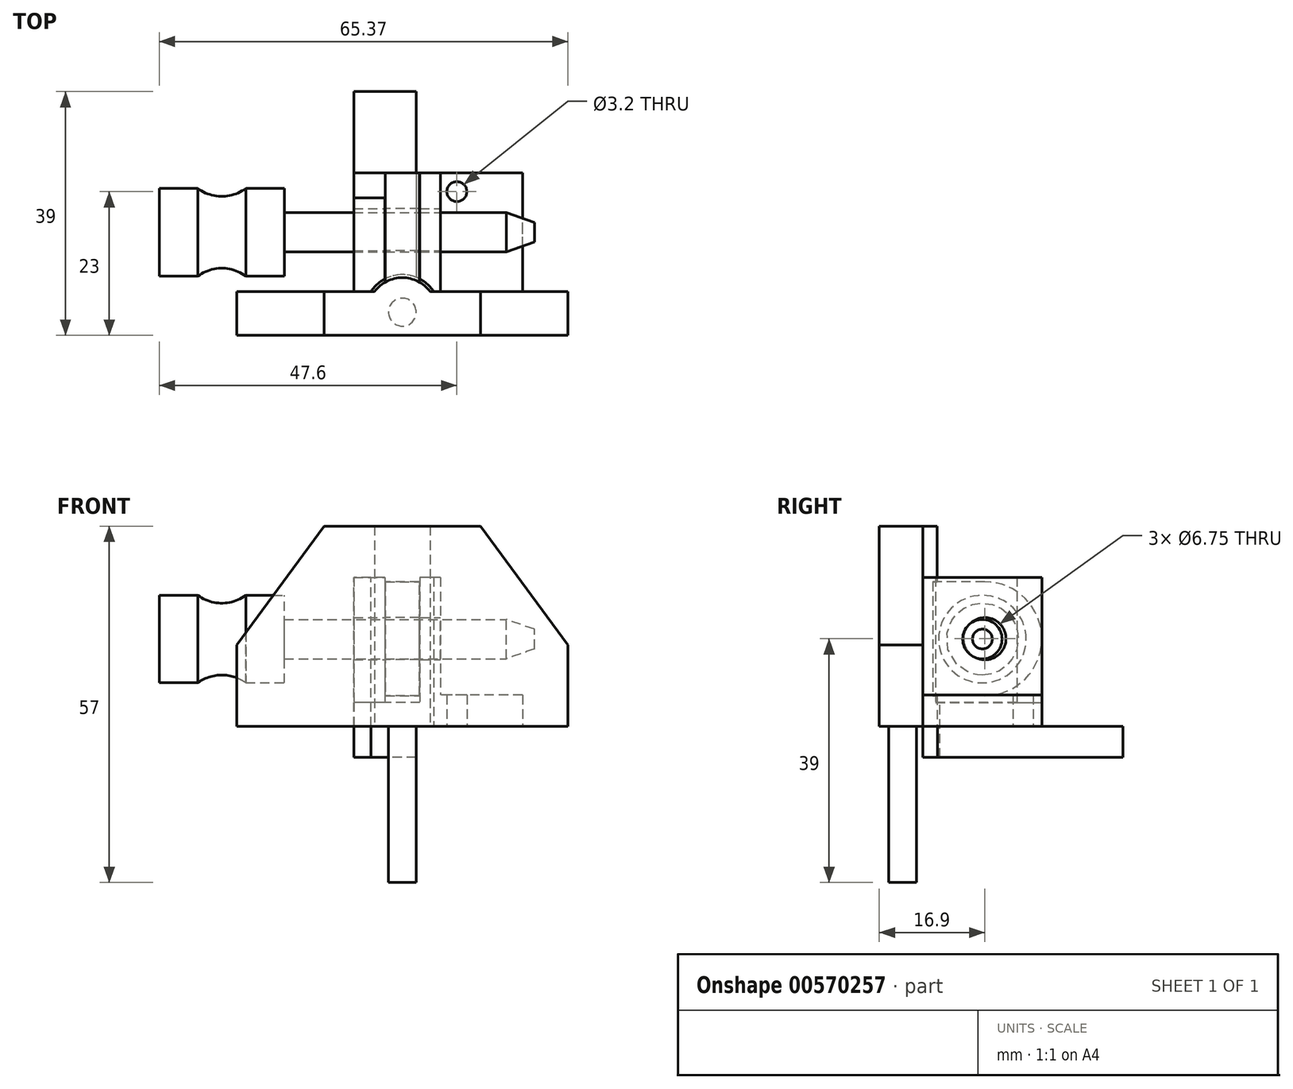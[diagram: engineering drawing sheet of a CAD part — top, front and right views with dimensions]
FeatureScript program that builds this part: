
annotation { "Feature Type Name" : "Feature", "Feature Type Description" : "" }
export const myFeature = defineFeature(function(context is Context, id is Id, definition is map)
    precondition{}
    {
        {
            var Q0;
            Q0=qCreatedBy(makeId("Top.planeOp"),FACE);
            var sketch = newSketch(context, id + "F0", { "sketchPlane" : qUnion([Q0])});
            skCircle(sketch, "E0", {"center": v(-5.72, -12.78) * mm, "radius": 2.23 * mm});
            skLineSegment(sketch, "E1.top", {"start": v(20.78, -9.5) * mm, "end": v(-32.22, -9.5) * mm});
            skLineSegment(sketch, "E1.left", {"start": v(20.78, -16.5) * mm, "end": v(20.78, -9.5) * mm});
            skLineSegment(sketch, "E1.right", {"start": v(-32.22, -16.5) * mm, "end": v(-32.22, -9.5) * mm});
            skLineSegment(sketch, "E2", {"start": v(-5.72, -9.5) * mm, "end": v(-5.72, -36.34) * mm, "construction": true});
            skLineSegment(sketch, "E3", {"start": v(-32.22, -16.5) * mm, "end": v(20.78, -16.5) * mm});
            skArc(sketch, "E4", {"start": v(-1.29, -9.5) * mm, "mid": v(-5.72, -7.26) * mm, "end": v(-10.16, -9.5) * mm});
            skSolve(sketch);
        }
        {
            var Q0;
            Q0=makeQuery(id+"F0.imprint","IMPRINT",FACE,{"disambiguationData":[TD([[makeQuery(id+"F0.imprint","IMPRINT",EDGE,{"derivedFrom":sQuery(id+"F0.wireOp",EDGE,"E0")}),-1.0]])]});
            var Q1;
            Q1=makeQuery(id+"F0.imprint","IMPRINT",FACE,{"disambiguationData":[TD([[makeQuery(id+"F0.imprint","IMPRINT",EDGE,{"derivedFrom":sQuery(id+"F0.wireOp",EDGE,"E0")}),1.0]])]});
            var Q2;
            {var subQ0=sQuery(id+"F0.wireOp",EDGE,"E4");Q2=makeQuery(id+"F0.imprint","IMPRINT",FACE,{"disambiguationData":[TD([[makeQuery(id+"F0.imprint","IMPRINT",EDGE,{"derivedFrom":subQ0}),1.0]])]});}
            extrude(context, id + "F1", {"entities" : qUnion([Q0, Q1, Q2]), "depth" : (19 + 13) * mm, "offsetDistance" : 25 * mm});
        }
        {
            var Q0;
            Q0=makeQuery(id+"F1.opExtrude","CAP_EDGE",EDGE,{"disambiguationData":[OSD([sQuery(id+"F0.wireOp",EDGE,"E1.right")])],"isStart":false});
            var Q1;
            Q1=makeQuery(id+"F1.opExtrude","CAP_EDGE",EDGE,{"disambiguationData":[OSD([sQuery(id+"F0.wireOp",EDGE,"E1.left")])],"isStart":false});
            chamfer(context, id + "F2", {"entities" : qUnion([Q0, Q1]), "chamferType" : ChamferType.TWO_OFFSETS, "width1" : 19 * mm, "oppositeDirection" : false, "width2" : 14 * mm, "tangentPropagation" : true});
        }
        {
            var Q0;
            Q0=makeQuery(id+"F0.imprint","IMPRINT",FACE,{"disambiguationData":[TD([[makeQuery(id+"F0.imprint","IMPRINT",EDGE,{"derivedFrom":sQuery(id+"F0.wireOp",EDGE,"E0")}),1.0]])]});
            extrude(context, id + "F3", {"entities" : qUnion([Q0]), "operationType" : NewBodyOperationType.ADD, "oppositeDirection" : true, "depth" : 25 * mm, "offsetDistance" : 25 * mm});
        }
        {
            var Q0;
            Q0=qCreatedBy(makeId("Right.planeOp"),FACE);
            var Q1;
            Q1=sQuery(id+"F0.wireOp",VERTEX,"E0.center");
            cPlane(context, id + "F4", {"entities" : qUnion([Q0, Q1]), "cplaneType" : CPlaneType.PLANE_POINT, "offset" : 25 * mm, "oppositeDirection" : true, "width" : 150 * mm, "height" : 150 * mm});
        }
        {
            var Q0;
            Q0=qCreatedBy(id+"F4.planeOp",FACE);
            var sketch = newSketch(context, id + "F5", { "sketchPlane" : qUnion([Q0])});
            skLineSegment(sketch, "E5.1", {"start": v(-16.5, 0) * mm, "end": v(-9.5, 0) * mm});
            skLineSegment(sketch, "E6.bottom", {"start": v(0.4, 23.1) * mm, "end": v(-16.5, 23.1) * mm});
            skLineSegment(sketch, "E6.top", {"start": v(0.4, 4) * mm, "end": v(-16.5, 4) * mm});
            skArc(sketch, "E7", {"start": v(0.4, 4.9) * mm, "mid": v(9.5, 14) * mm, "end": v(0.4, 23.1) * mm});
            skCircle(sketch, "E8", {"center": v(0.4, 14) * mm, "radius": 3.38 * mm});
            skLineSegment(sketch, "E9.0", {"start": v(-16.5, 13) * mm, "end": v(-16.5, 0) * mm});
            skLineSegment(sketch, "E9.1", {"start": v(-16.5, 13) * mm, "end": v(-16.5, 32) * mm});
            skLineSegment(sketch, "E10.0", {"start": v(0.4, 4.9) * mm, "end": v(-16.5, 4.9) * mm});
            skLineSegment(sketch, "E11.0", {"start": v(-9.5, 32) * mm, "end": v(-9.5, 13) * mm, "construction": true});
            skLineSegment(sketch, "E11.1", {"start": v(-9.5, 13) * mm, "end": v(-9.5, 0) * mm, "construction": true});
            skSolve(sketch);
        }
        {
            var Q0;
            Q0 = qSketchRegion(id + "F5", true);
            extrude(context, id + "F6", {"entities" : qUnion([Q0]), "operationType" : NewBodyOperationType.ADD, "depth" : 5.4 * mm, "offsetDistance" : 25 * mm, "symmetric" : true});
        }
        {
            var Q0;
            Q0=qCreatedBy(makeId("Top.planeOp"),FACE);
            var sketch = newSketch(context, id + "F7", { "sketchPlane" : qUnion([Q0])});
            skLineSegment(sketch, "E12.bottom", {"start": v(13.5, -9.5) * mm, "end": v(-13.5, -9.5) * mm});
            skLineSegment(sketch, "E12.left", {"start": v(13.5, -9.5) * mm, "end": v(13.5, 9.5) * mm});
            skLineSegment(sketch, "E12.right", {"start": v(-13.5, -9.5) * mm, "end": v(-13.5, 9.5) * mm});
            skPoint(sketch, "E12.middle", {"position": v(0, 0) * mm});
            skCircle(sketch, "E13", {"center": v(3, 6.5) * mm, "radius": 1.6 * mm});
            skLineSegment(sketch, "E14", {"start": v(-3.5, 9.5) * mm, "end": v(-3.5, -7.2) * mm});
            skArc(sketch, "E15", {"start": v(-0.7, -9.5) * mm, "mid": v(-5.72, -6.78) * mm, "end": v(-10.75, -9.5) * mm});
            skLineSegment(sketch, "E16", {"start": v(-13.5, 22.5) * mm, "end": v(-3.5, 22.5) * mm});
            skLineSegment(sketch, "E17", {"start": v(13.5, 9.5) * mm, "end": v(-13.5, 9.5) * mm});
            skLineSegment(sketch, "E18", {"start": v(-13.5, 22.5) * mm, "end": v(-13.5, 9.5) * mm});
            skLineSegment(sketch, "E19", {"start": v(-3.5, 22.5) * mm, "end": v(-3.5, 9.5) * mm});
            skCircle(sketch, "E20", {"center": v(3, 6.5) * mm, "radius": 2.6 * mm, "construction": true});
            skLineSegment(sketch, "E21", {"start": v(0.4, 9.5) * mm, "end": v(0.4, -9.5) * mm});
            skLineSegment(sketch, "E22", {"start": v(-2.92, 9.5) * mm, "end": v(-2.92, -7.47) * mm});
            skLineSegment(sketch, "E23", {"start": v(-8.52, -7.47) * mm, "end": v(-8.52, 9.5) * mm});
            skLineSegment(sketch, "E24", {"start": v(-13.5, 5.5) * mm, "end": v(-8.52, 5.5) * mm});
            skSolve(sketch);
        }
        {
            var Q0;
            Q0=makeQuery(id+"F7.imprint","IMPRINT",FACE,{"disambiguationData":[TD([[makeQuery(id+"F7.imprint","IMPRINT",EDGE,{"derivedFrom":sQuery(id+"F7.wireOp",EDGE,"E16")}),-1.0]])]});
            var Q1;
            {var subQ5=sQuery(id+"F7.wireOp",EDGE,"E14");Q1=makeQuery(id+"F7.imprint","IMPRINT",FACE,{"disambiguationData":[TD([[makeQuery(id+"F7.imprint","IMPRINT",EDGE,{"derivedFrom":subQ5}),-1.0]])]});}
            var Q2;
            {var subQ1=sQuery(id+"F7.wireOp",EDGE,"E12.right");Q2=makeQuery(id+"F7.imprint","IMPRINT",FACE,{"disambiguationData":[TD([[makeQuery(id+"F7.imprint","IMPRINT",EDGE,{"derivedFrom":subQ1}),-1.0]])]});}
            var Q3;
            {var subQ5=sQuery(id+"F7.wireOp",EDGE,"E24");Q3=makeQuery(id+"F7.imprint","IMPRINT",FACE,{"disambiguationData":[TD([[makeQuery(id+"F7.imprint","IMPRINT",EDGE,{"derivedFrom":subQ5}),-1.0]])]});}
            extrude(context, id + "F8", {"entities" : qUnion([Q0, Q1, Q2, Q3]), "oppositeDirection" : true, "depth" : 5 * mm, "offsetDistance" : 25 * mm});
        }
        {
            var Q0;
            {var subQ0=sQuery(id+"F7.wireOp",EDGE,"E14");Q0=makeQuery(id+"F7.imprint","IMPRINT",FACE,{"disambiguationData":[TD([[makeQuery(id+"F7.imprint","IMPRINT",EDGE,{"derivedFrom":subQ0}),-1.0]])]});}
            var Q1;
            {var subQ0=sQuery(id+"F7.wireOp",EDGE,"E14");Q1=makeQuery(id+"F7.imprint","IMPRINT",FACE,{"disambiguationData":[TD([[makeQuery(id+"F7.imprint","IMPRINT",EDGE,{"derivedFrom":subQ0}),1.0]])]});}
            var Q2;
            {var subQ0=sQuery(id+"F7.wireOp",EDGE,"E21");Q2=makeQuery(id+"F7.imprint","IMPRINT",FACE,{"disambiguationData":[TD([[makeQuery(id+"F7.imprint","IMPRINT",EDGE,{"derivedFrom":subQ0}),-1.0]])]});}
            var Q3;
            {var subQ1=sQuery(id+"F7.wireOp",EDGE,"E12.right");Q3=makeQuery(id+"F7.imprint","IMPRINT",FACE,{"disambiguationData":[TD([[makeQuery(id+"F7.imprint","IMPRINT",EDGE,{"derivedFrom":subQ1}),-1.0]])]});}
            var Q4;
            {var subQ5=sQuery(id+"F7.wireOp",EDGE,"E24");Q4=makeQuery(id+"F7.imprint","IMPRINT",FACE,{"disambiguationData":[TD([[makeQuery(id+"F7.imprint","IMPRINT",EDGE,{"derivedFrom":subQ5}),-1.0]])]});}
            var Q5;
            Q5=makeQuery(id+"F1.opExtrude","SWEPT_BODY",BODY,{"disambiguationData":[OSD([sQuery(id+"F0.wireOp",EDGE,"E1.top"),sQuery(id+"F0.wireOp",EDGE,"E1.left"),sQuery(id+"F0.wireOp",EDGE,"E1.right"),sQuery(id+"F0.wireOp",EDGE,"E3"),sQuery(id+"F0.wireOp",EDGE,"E4")])]});
            extrude(context, id + "F9", {"entities" : qUnion([Q0, Q1, Q2, Q3, Q4]), "operationType" : NewBodyOperationType.ADD, "depth" : 3.8 * mm, "endBoundEntityBody" : qUnion([Q5]), "offsetDistance" : 25 * mm});
        }
        {
            var Q0;
            {var subQ1=sQuery(id+"F7.wireOp",EDGE,"E12.left");Q0=makeQuery(id+"F7.imprint","IMPRINT",FACE,{"disambiguationData":[TD([[makeQuery(id+"F7.imprint","IMPRINT",EDGE,{"derivedFrom":subQ1}),1.0]])]});}
            extrude(context, id + "F10", {"entities" : qUnion([Q0]), "operationType" : NewBodyOperationType.ADD, "depth" : 5 * mm, "offsetDistance" : 25 * mm});
        }
        {
            var Q0;
            {var subQ5=sQuery(id+"F7.wireOp",EDGE,"E24");Q0=makeQuery(id+"F7.imprint","IMPRINT",FACE,{"disambiguationData":[TD([[makeQuery(id+"F7.imprint","IMPRINT",EDGE,{"derivedFrom":subQ5}),-1.0]])]});}
            var Q1;
            {var subQ0=sQuery(id+"F7.wireOp",EDGE,"E21");Q1=makeQuery(id+"F7.imprint","IMPRINT",FACE,{"disambiguationData":[TD([[makeQuery(id+"F7.imprint","IMPRINT",EDGE,{"derivedFrom":subQ0}),-1.0]])]});}
            extrude(context, id + "F11", {"entities" : qUnion([Q0, Q1]), "operationType" : NewBodyOperationType.ADD, "depth" : 23.8 * mm, "offsetDistance" : 25 * mm});
        }
        {
            var Q0;
            Q0=makeQuery(id+"F11.opExtrude","SWEPT_FACE",FACE,{"disambiguationData":[OSD([sQuery(id+"F7.wireOp",EDGE,"E21")])]});
            var sketch = newSketch(context, id + "F12", { "sketchPlane" : qUnion([Q0])});
            skCircle(sketch, "E25.0", {"center": v(0.4, 14) * mm, "radius": 3.38 * mm});
            skSolve(sketch);
        }
        {
            var Q0;
            Q0=makeQuery(id+"F12.imprint","IMPRINT",FACE,{"disambiguationData":[TD([[makeQuery(id+"F12.imprint","IMPRINT",EDGE,{"derivedFrom":sQuery(id+"F12.wireOp",EDGE,"E25.0")}),1.0]])]});
            var Q1;
            {var subQ0=sQuery(id+"F7.wireOp",EDGE,"E12.right");Q1=makeQuery(id+"FuMEe041B781IBN_2.boolean.opBoolean","MERGE",FACE,{"derivedFrom":[makeQuery(id+"F9.boolean.opBoolean","MERGE",FACE,{"derivedFrom":[makeQuery(id+"F8.opExtrude","SWEPT_FACE",FACE,{"disambiguationData":[OSD([subQ0,sQuery(id+"F7.wireOp",EDGE,"KzPBEShh-w5PI-gnjr-G1oW-jOOn24wAJrg6")])]}),makeQuery(id+"F9.opExtrude","SWEPT_FACE",FACE,{"disambiguationData":[OSD([subQ0])]})]}),makeQuery(id+"FuMEe041B781IBN_2.opExtrude","SWEPT_FACE",FACE,{"disambiguationData":[OSD([sQuery(id+"FgnUgKHV0ezVjLo_2.wireOp",EDGE,"6809b705-6927-40f1-b6ce-b852e40d2108.0")])]})]});}
            extrude(context, id + "F13", {"entities" : qUnion([Q0]), "operationType" : NewBodyOperationType.REMOVE, "endBound" : BoundingType.UP_TO_SURFACE, "oppositeDirection" : true, "depth" : 25 * mm, "endBoundEntityFace" : qUnion([Q1]), "offsetDistance" : 25 * mm});
        }
        {
            var Q0;
            Q0=qCreatedBy(makeId("Front.planeOp"),FACE);
            var sketch = newSketch(context, id + "F14", { "sketchPlane" : qUnion([Q0])});
            skLineSegment(sketch, "E26.bottom", {"start": v(10.9, 17.09) * mm, "end": v(-24.6, 17.09) * mm});
            skLineSegment(sketch, "E26.top", {"start": v(15.4, 13.94) * mm, "end": v(-24.6, 13.94) * mm});
            skLineSegment(sketch, "E26.left", {"start": v(15.4, 15.51) * mm, "end": v(15.4, 13.94) * mm});
            skLineSegment(sketch, "E26.right", {"start": v(-24.6, 17.09) * mm, "end": v(-24.6, 13.94) * mm});
            skLineSegment(sketch, "E27", {"start": v(15.4, 15.51) * mm, "end": v(10.9, 17.09) * mm});
            skLineSegment(sketch, "E28.bottom", {"start": v(-24.6, 20.94) * mm, "end": v(-30.77, 20.94) * mm});
            skLineSegment(sketch, "E28.top", {"start": v(-24.6, 13.94) * mm, "end": v(-44.6, 13.94) * mm});
            skLineSegment(sketch, "E28.left", {"start": v(-24.6, 20.94) * mm, "end": v(-24.6, 13.94) * mm});
            skLineSegment(sketch, "E28.right", {"start": v(-44.6, 20.94) * mm, "end": v(-44.6, 13.94) * mm});
            skArc(sketch, "E29", {"start": v(-38.43, 20.94) * mm, "mid": v(-34.6, 19.69) * mm, "end": v(-30.77, 20.94) * mm});
            skLineSegment(sketch, "E30.trimOffspring", {"start": v(-38.43, 20.94) * mm, "end": v(-44.6, 20.94) * mm});
            skLineSegment(sketch, "E31", {"start": v(-34.6, 13.94) * mm, "end": v(-34.6, 32.41) * mm, "construction": true});
            skSolve(sketch);
        }
        {
            var Q0;
            {var subQ1=sQuery(id+"F14.wireOp",EDGE,"E26.bottom");Q0=makeQuery(id+"F14.imprint","IMPRINT",FACE,{"disambiguationData":[TD([[makeQuery(id+"F14.imprint","IMPRINT",EDGE,{"derivedFrom":subQ1}),1.0]])]});}
            var Q1;
            {var subQ3=sQuery(id+"F14.wireOp",EDGE,"E28.bottom");Q1=makeQuery(id+"F14.imprint","IMPRINT",FACE,{"disambiguationData":[TD([[makeQuery(id+"F14.imprint","IMPRINT",EDGE,{"derivedFrom":subQ3}),1.0]])]});}
            var Q2;
            Q2=sQuery(id+"F14.wireOp",EDGE,"E26.top");
            revolve(context, id + "F15", {"entities" : qUnion([Q0, Q1]), "axis" : qUnion([Q2]), "revolveType" : RevolveType.FULL});
        }
    });
